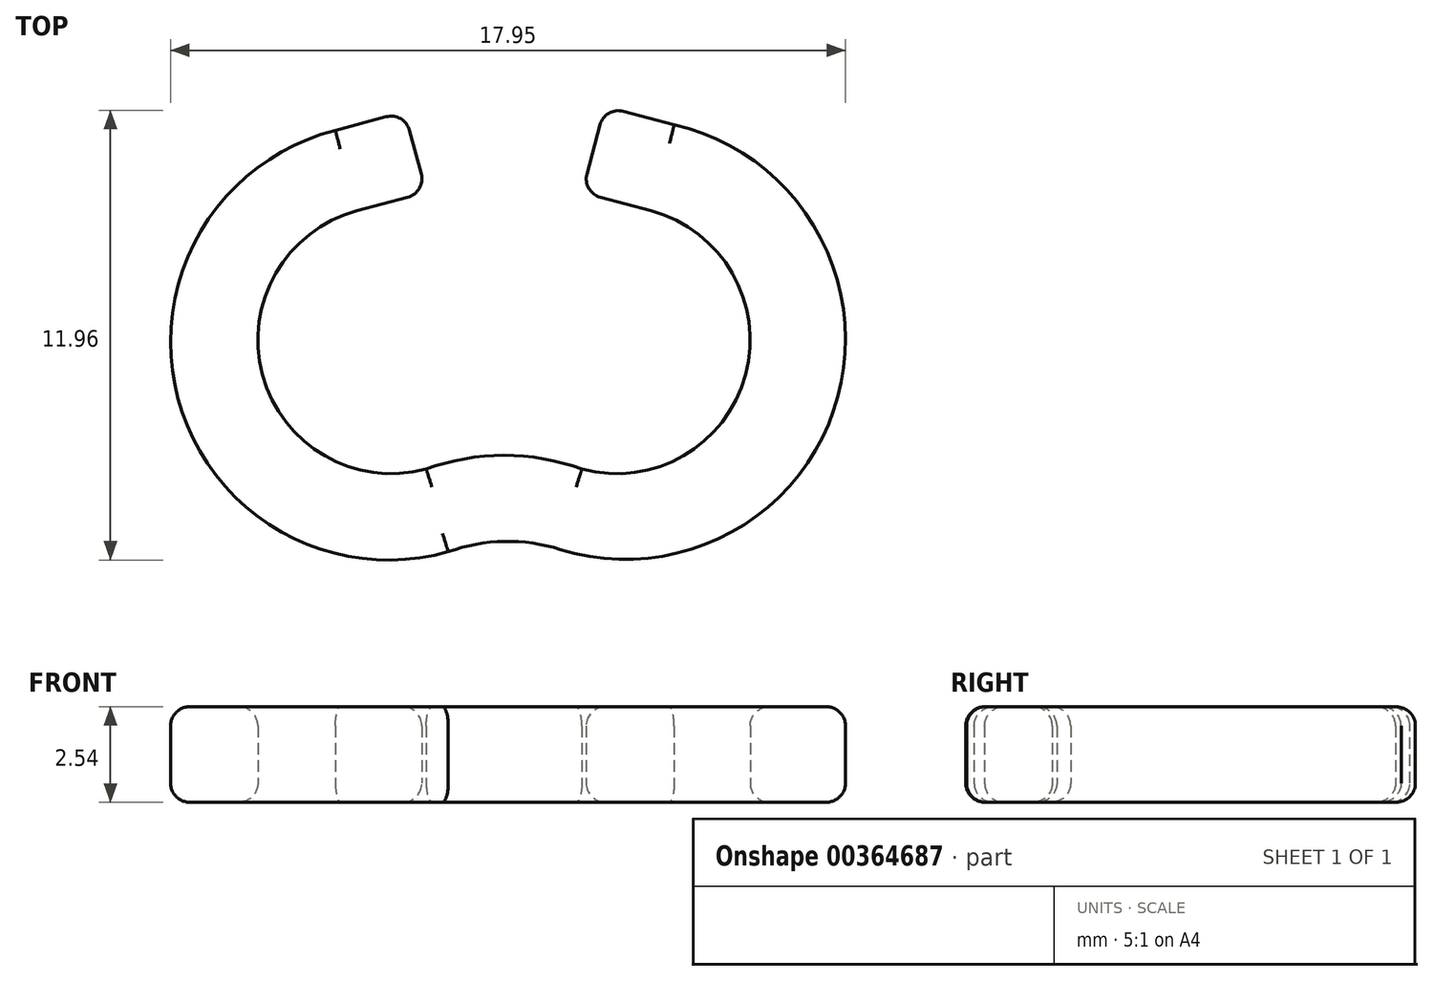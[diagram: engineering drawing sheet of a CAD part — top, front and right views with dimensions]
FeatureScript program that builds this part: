
annotation { "Feature Type Name" : "Feature", "Feature Type Description" : "" }
export const myFeature = defineFeature(function(context is Context, id is Id, definition is map)
    precondition{}
    {
        {
            var Q0;
            Q0=qCreatedBy(makeId("Top.planeOp"),FACE);
            var sketch = newSketch(context, id + "F0", { "sketchPlane" : qUnion([Q0])});
            skPoint(sketch, "E0.centerSnap0", {"position": v(-1.9, -0.04) * mm});
            skPoint(sketch, "E1.centerSnap0", {"position": v(1.9, -0.04) * mm});
            skArc(sketch, "E2", {"start": v(-4.48, 4.93) * mm, "mid": v(-8.67, -2.2) * mm, "end": v(-1.48, -6.28) * mm});
            skArc(sketch, "E3", {"start": v(1.5, -6.22) * mm, "mid": v(8.88, -2.14) * mm, "end": v(4.52, 5.08) * mm});
            skLineSegment(sketch, "E4", {"start": v(-4.48, 4.93) * mm, "end": v(-2.64, 5.42) * mm});
            skLineSegment(sketch, "E5", {"start": v(4.52, 5.08) * mm, "end": v(2.68, 5.57) * mm});
            skLineSegment(sketch, "E6", {"start": v(-2.07, 3.28) * mm, "end": v(-2.64, 5.42) * mm});
            skLineSegment(sketch, "E7", {"start": v(2.07, 3.28) * mm, "end": v(2.68, 5.57) * mm});
            skLineSegment(sketch, "E8.0", {"start": v(-3.91, 2.8) * mm, "end": v(-2.07, 3.28) * mm});
            skLineSegment(sketch, "E9.0", {"start": v(3.91, 2.8) * mm, "end": v(2.07, 3.28) * mm});
            skArc(sketch, "E10", {"start": v(-3.91, 2.8) * mm, "mid": v(-6.43, -1.56) * mm, "end": v(-2.07, -4.08) * mm});
            skArc(sketch, "E11", {"start": v(2.07, -4.08) * mm, "mid": v(6.43, -1.56) * mm, "end": v(3.91, 2.8) * mm});
            skArc(sketch, "E12", {"start": v(2.07, -4.08) * mm, "mid": v(0, -3.71) * mm, "end": v(-2.07, -4.08) * mm});
            skArc(sketch, "E13", {"start": v(1.5, -6.22) * mm, "mid": v(0, -6) * mm, "end": v(-1.48, -6.28) * mm});
            skSolve(sketch);
        }
        {
            var Q0;
            Q0=makeQuery(id+"F0.imprint","IMPRINT",FACE,{"disambiguationData":[TD([[makeQuery(id+"F0.imprint","IMPRINT",EDGE,{"derivedFrom":sQuery(id+"F0.wireOp",EDGE,"E2")}),1.0]])]});
            extrude(context, id + "F1", {"entities" : qUnion([Q0]), "depth" : 2.54 * mm});
        }
        {
            var Q0;
            Q0=makeQuery(id+"F1.opExtrude","CAP_FACE",FACE,{"disambiguationData":[OSD([sQuery(id+"F0.wireOp",EDGE,"E2"),sQuery(id+"F0.wireOp",EDGE,"E3"),sQuery(id+"F0.wireOp",EDGE,"E4"),sQuery(id+"F0.wireOp",EDGE,"E5"),sQuery(id+"F0.wireOp",EDGE,"E6"),sQuery(id+"F0.wireOp",EDGE,"E7"),sQuery(id+"F0.wireOp",EDGE,"E8.0"),sQuery(id+"F0.wireOp",EDGE,"E9.0"),sQuery(id+"F0.wireOp",EDGE,"E10"),sQuery(id+"F0.wireOp",EDGE,"E11"),sQuery(id+"F0.wireOp",EDGE,"E12"),sQuery(id+"F0.wireOp",EDGE,"E13")])],"isStart":false});
            var Q1;
            Q1=makeQuery(id+"F1.opExtrude","CAP_FACE",FACE,{"disambiguationData":[OSD([sQuery(id+"F0.wireOp",EDGE,"E2"),sQuery(id+"F0.wireOp",EDGE,"E3"),sQuery(id+"F0.wireOp",EDGE,"E4"),sQuery(id+"F0.wireOp",EDGE,"E5"),sQuery(id+"F0.wireOp",EDGE,"E6"),sQuery(id+"F0.wireOp",EDGE,"E7"),sQuery(id+"F0.wireOp",EDGE,"E8.0"),sQuery(id+"F0.wireOp",EDGE,"E9.0"),sQuery(id+"F0.wireOp",EDGE,"E10"),sQuery(id+"F0.wireOp",EDGE,"E11"),sQuery(id+"F0.wireOp",EDGE,"E12"),sQuery(id+"F0.wireOp",EDGE,"E13")])],"isStart":true});
            var Q2;
            Q2=makeQuery(id+"F1.opExtrude","SWEPT_FACE",FACE,{"disambiguationData":[OSD([sQuery(id+"F0.wireOp",EDGE,"E6")])]});
            var Q3;
            Q3=makeQuery(id+"F1.opExtrude","SWEPT_FACE",FACE,{"disambiguationData":[OSD([sQuery(id+"F0.wireOp",EDGE,"E7")])]});
            fillet(context, id + "F2", {"entities" : qUnion([Q0, Q1, Q2, Q3]), "radius" : 0.5 * mm, "tangentPropagation" : true, "allowEdgeOverflow" : false});
        }
    });
